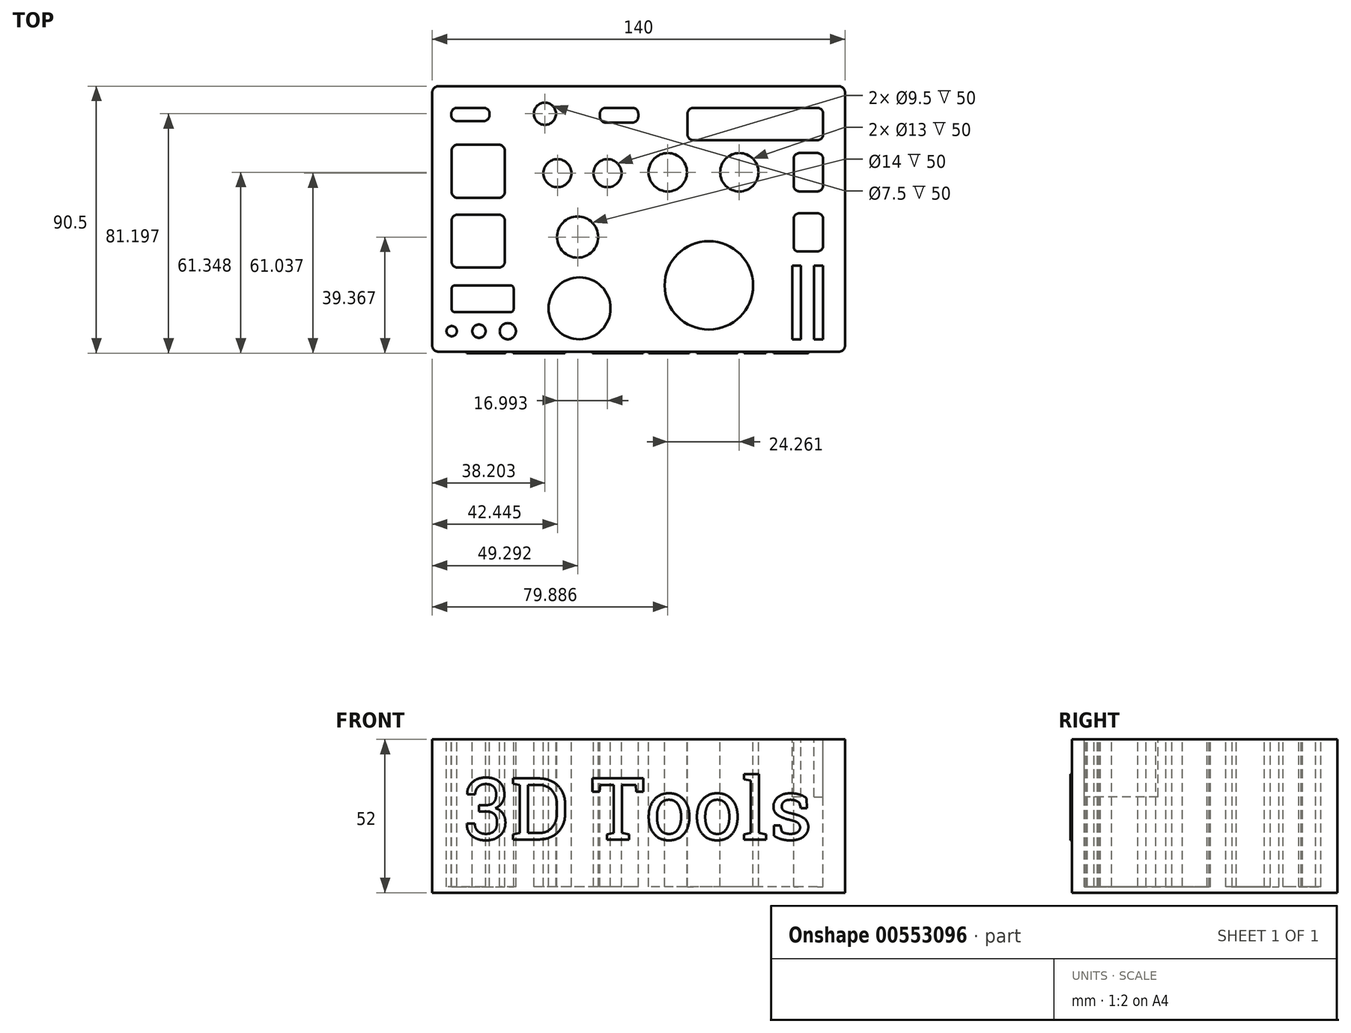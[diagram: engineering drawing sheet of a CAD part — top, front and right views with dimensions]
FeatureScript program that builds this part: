
annotation { "Feature Type Name" : "Feature", "Feature Type Description" : "" }
export const myFeature = defineFeature(function(context is Context, id is Id, definition is map)
    precondition{}
    {
        {
            var Q0;
            Q0=qCreatedBy(makeId("Top.planeOp"),FACE);
            var sketch = newSketch(context, id + "F0", { "sketchPlane" : qUnion([Q0])});
            skLineSegment(sketch, "E0.bottom", {"start": v(-68, 44) * mm, "end": v(68, 44) * mm});
            skLineSegment(sketch, "E0.top", {"start": v(-68, -46) * mm, "end": v(68, -46) * mm});
            skLineSegment(sketch, "E0.left", {"start": v(-70, 42) * mm, "end": v(-70, -44) * mm});
            skLineSegment(sketch, "E0.right", {"start": v(70, 42) * mm, "end": v(70, -44) * mm});
            skCircle(sketch, "E1", {"center": v(-20.04, -31.3) * mm, "radius": 10.5 * mm});
            skLineSegment(sketch, "E2.bottom", {"start": v(60.58, -12.03) * mm, "end": v(54.16, -12.03) * mm});
            skLineSegment(sketch, "E2.top", {"start": v(60.58, 0.97) * mm, "end": v(54.58, 0.97) * mm});
            skLineSegment(sketch, "E2.left", {"start": v(62.58, -10.03) * mm, "end": v(62.58, -1.03) * mm});
            skLineSegment(sketch, "E2.right", {"start": v(52.58, -10.45) * mm, "end": v(52.58, -1.03) * mm});
            skPoint(sketch, "E2.middle", {"position": v(57.58, -5.53) * mm});
            skLineSegment(sketch, "E3.bottom", {"start": v(60.58, 36.7) * mm, "end": v(18.58, 36.7) * mm});
            skLineSegment(sketch, "E3.top", {"start": v(60.58, 25.7) * mm, "end": v(18.58, 25.7) * mm});
            skLineSegment(sketch, "E3.left", {"start": v(62.58, 34.7) * mm, "end": v(62.58, 27.7) * mm});
            skLineSegment(sketch, "E3.right", {"start": v(16.58, 34.7) * mm, "end": v(16.58, 27.7) * mm});
            skPoint(sketch, "E4.visualSharp", {"position": v(16.58, 36.7) * mm});
            skArc(sketch, "E4.filletArc", {"start": v(18.58, 36.7) * mm, "mid": v(17.16, 36.11) * mm, "end": v(16.58, 34.7) * mm});
            skPoint(sketch, "E5.visualSharp", {"position": v(16.58, 25.7) * mm});
            skArc(sketch, "E5.filletArc", {"start": v(16.58, 27.7) * mm, "mid": v(17.16, 26.28) * mm, "end": v(18.58, 25.7) * mm});
            skPoint(sketch, "E6.visualSharp", {"position": v(62.58, 25.7) * mm});
            skArc(sketch, "E6.filletArc", {"start": v(60.58, 25.7) * mm, "mid": v(62, 26.28) * mm, "end": v(62.58, 27.7) * mm});
            skPoint(sketch, "E7.visualSharp", {"position": v(62.58, 36.7) * mm});
            skArc(sketch, "E7.filletArc", {"start": v(62.58, 34.7) * mm, "mid": v(62, 36.11) * mm, "end": v(60.58, 36.7) * mm});
            skPoint(sketch, "E8.visualSharp", {"position": v(62.58, 0.97) * mm});
            skArc(sketch, "E8.filletArc", {"start": v(62.58, -1.03) * mm, "mid": v(62, 0.39) * mm, "end": v(60.58, 0.97) * mm});
            skPoint(sketch, "E9.visualSharp", {"position": v(52.58, 0.97) * mm});
            skArc(sketch, "E9.filletArc", {"start": v(54.58, 0.97) * mm, "mid": v(53.16, 0.39) * mm, "end": v(52.58, -1.03) * mm});
            skPoint(sketch, "E10.visualSharp", {"position": v(52.58, -12.03) * mm});
            skArc(sketch, "E10.filletArc", {"start": v(52.58, -10.45) * mm, "mid": v(53.04, -11.56) * mm, "end": v(54.16, -12.03) * mm});
            skPoint(sketch, "E11.visualSharp", {"position": v(62.58, -12.03) * mm});
            skArc(sketch, "E11.filletArc", {"start": v(60.58, -12.03) * mm, "mid": v(62, -11.44) * mm, "end": v(62.58, -10.03) * mm});
            skPoint(sketch, "E12.visualSharp", {"position": v(-70, 44) * mm});
            skArc(sketch, "E12.filletArc", {"start": v(-68, 44) * mm, "mid": v(-69.41, 43.41) * mm, "end": v(-70, 42) * mm});
            skPoint(sketch, "E13.visualSharp", {"position": v(70, 44) * mm});
            skArc(sketch, "E13.filletArc", {"start": v(70, 42) * mm, "mid": v(69.41, 43.41) * mm, "end": v(68, 44) * mm});
            skPoint(sketch, "E14.endSnap0", {"position": v(52.58, -5.74) * mm});
            skPoint(sketch, "E15.endSnap0", {"position": v(57.58, 0.97) * mm});
            skPoint(sketch, "E16.endSnap0", {"position": v(16.58, 31.2) * mm});
            skCircle(sketch, "E17", {"center": v(-20.7, -7.13) * mm, "radius": 7 * mm});
            skCircle(sketch, "E18", {"center": v(-10.56, 14.54) * mm, "radius": 4.75 * mm});
            skLineSegment(sketch, "E19.bottom", {"start": v(60.58, 8.35) * mm, "end": v(54.58, 8.35) * mm});
            skLineSegment(sketch, "E19.top", {"start": v(60.58, 21.35) * mm, "end": v(54.58, 21.35) * mm});
            skLineSegment(sketch, "E19.left", {"start": v(62.58, 10.35) * mm, "end": v(62.58, 19.35) * mm});
            skLineSegment(sketch, "E19.right", {"start": v(52.58, 10.35) * mm, "end": v(52.58, 19.35) * mm});
            skPoint(sketch, "E20.visualSharp", {"position": v(52.58, 21.35) * mm});
            skArc(sketch, "E20.filletArc", {"start": v(54.58, 21.35) * mm, "mid": v(53.16, 20.76) * mm, "end": v(52.58, 19.35) * mm});
            skPoint(sketch, "E21.visualSharp", {"position": v(62.58, 21.35) * mm});
            skArc(sketch, "E21.filletArc", {"start": v(62.58, 19.35) * mm, "mid": v(62, 20.76) * mm, "end": v(60.58, 21.35) * mm});
            skPoint(sketch, "E22.visualSharp", {"position": v(62.58, 8.35) * mm});
            skArc(sketch, "E22.filletArc", {"start": v(60.58, 8.35) * mm, "mid": v(62, 8.93) * mm, "end": v(62.58, 10.35) * mm});
            skPoint(sketch, "E23.visualSharp", {"position": v(52.58, 8.35) * mm});
            skArc(sketch, "E23.filletArc", {"start": v(52.58, 10.35) * mm, "mid": v(53.16, 8.93) * mm, "end": v(54.58, 8.35) * mm});
            skCircle(sketch, "E24", {"center": v(23.83, -23.52) * mm, "radius": 15 * mm});
            skCircle(sketch, "E25", {"center": v(34.15, 14.85) * mm, "radius": 6.5 * mm});
            skCircle(sketch, "E26", {"center": v(9.89, 14.85) * mm, "radius": 6.5 * mm});
            skCircle(sketch, "E27", {"center": v(-63.43, -39.06) * mm, "radius": 1.75 * mm});
            skLineSegment(sketch, "E28.bottom", {"start": v(-61.43, 0.5) * mm, "end": v(-47.43, 0.5) * mm});
            skLineSegment(sketch, "E28.top", {"start": v(-61.43, -17.5) * mm, "end": v(-47.43, -17.5) * mm});
            skLineSegment(sketch, "E28.left", {"start": v(-63.43, -1.5) * mm, "end": v(-63.43, -15.5) * mm});
            skLineSegment(sketch, "E28.right", {"start": v(-45.43, -1.5) * mm, "end": v(-45.43, -15.5) * mm});
            skPoint(sketch, "E29.visualSharp", {"position": v(-63.43, 0.5) * mm});
            skArc(sketch, "E29.filletArc", {"start": v(-61.43, 0.5) * mm, "mid": v(-62.84, -0.1) * mm, "end": v(-63.43, -1.5) * mm});
            skPoint(sketch, "E30.visualSharp", {"position": v(-63.43, -17.5) * mm});
            skArc(sketch, "E30.filletArc", {"start": v(-63.43, -15.5) * mm, "mid": v(-62.84, -16.92) * mm, "end": v(-61.43, -17.5) * mm});
            skPoint(sketch, "E31.visualSharp", {"position": v(-45.43, -17.5) * mm});
            skArc(sketch, "E31.filletArc", {"start": v(-47.43, -17.5) * mm, "mid": v(-46.01, -16.92) * mm, "end": v(-45.43, -15.5) * mm});
            skPoint(sketch, "E32.visualSharp", {"position": v(-45.43, 0.5) * mm});
            skArc(sketch, "E32.filletArc", {"start": v(-45.43, -1.5) * mm, "mid": v(-46.01, -0.1) * mm, "end": v(-47.43, 0.5) * mm});
            skPoint(sketch, "E33.visualSharp", {"position": v(-70, -46) * mm});
            skArc(sketch, "E33.filletArc", {"start": v(-70, -44) * mm, "mid": v(-69.41, -45.41) * mm, "end": v(-68, -46) * mm});
            skPoint(sketch, "E34.visualSharp", {"position": v(70, -46) * mm});
            skArc(sketch, "E34.filletArc", {"start": v(68, -46) * mm, "mid": v(69.41, -45.41) * mm, "end": v(70, -44) * mm});
            skCircle(sketch, "E35", {"center": v(-54.16, -39.06) * mm, "radius": 2.25 * mm});
            skCircle(sketch, "E36", {"center": v(-44.38, -39.06) * mm, "radius": 2.75 * mm});
            skLineSegment(sketch, "E37.bottom", {"start": v(-61.43, 6.18) * mm, "end": v(-47.43, 6.18) * mm});
            skLineSegment(sketch, "E37.top", {"start": v(-61.43, 24.18) * mm, "end": v(-47.43, 24.18) * mm});
            skLineSegment(sketch, "E37.left", {"start": v(-63.43, 8.18) * mm, "end": v(-63.43, 22.18) * mm});
            skLineSegment(sketch, "E37.right", {"start": v(-45.43, 8.18) * mm, "end": v(-45.43, 22.18) * mm});
            skPoint(sketch, "E38.visualSharp", {"position": v(-63.43, 24.18) * mm});
            skArc(sketch, "E38.filletArc", {"start": v(-61.43, 24.18) * mm, "mid": v(-62.84, 23.6) * mm, "end": v(-63.43, 22.18) * mm});
            skPoint(sketch, "E39.visualSharp", {"position": v(-45.43, 24.18) * mm});
            skArc(sketch, "E39.filletArc", {"start": v(-45.43, 22.18) * mm, "mid": v(-46.01, 23.6) * mm, "end": v(-47.43, 24.18) * mm});
            skPoint(sketch, "E40.visualSharp", {"position": v(-45.43, 6.18) * mm});
            skArc(sketch, "E40.filletArc", {"start": v(-47.43, 6.18) * mm, "mid": v(-46.01, 6.77) * mm, "end": v(-45.43, 8.18) * mm});
            skPoint(sketch, "E41.visualSharp", {"position": v(-63.43, 6.18) * mm});
            skArc(sketch, "E41.filletArc", {"start": v(-63.43, 8.18) * mm, "mid": v(-62.84, 6.77) * mm, "end": v(-61.43, 6.18) * mm});
            skLineSegment(sketch, "E42", {"start": v(62.58, -10.03) * mm, "end": v(62.58, -10.17) * mm, "construction": true});
            skCircle(sketch, "E43", {"center": v(-27.55, 14.54) * mm, "radius": 4.75 * mm});
            skLineSegment(sketch, "E44.bottom", {"start": v(-52.59, 36.7) * mm, "end": v(-61.59, 36.7) * mm});
            skLineSegment(sketch, "E44.top", {"start": v(-52.59, 32.2) * mm, "end": v(-61.59, 32.2) * mm});
            skLineSegment(sketch, "E44.left", {"start": v(-50.59, 34.7) * mm, "end": v(-50.59, 34.2) * mm});
            skLineSegment(sketch, "E44.right", {"start": v(-63.59, 34.7) * mm, "end": v(-63.59, 34.2) * mm});
            skLineSegment(sketch, "E45.bottom", {"start": v(-2.13, 36.7) * mm, "end": v(-11.13, 36.7) * mm});
            skLineSegment(sketch, "E45.top", {"start": v(-2.13, 31.7) * mm, "end": v(-11.13, 31.7) * mm});
            skLineSegment(sketch, "E45.left", {"start": v(-0.13, 34.7) * mm, "end": v(-0.13, 33.7) * mm});
            skLineSegment(sketch, "E45.right", {"start": v(-13.13, 34.7) * mm, "end": v(-13.13, 33.7) * mm});
            skPoint(sketch, "E46.visualSharp", {"position": v(-13.13, 36.7) * mm});
            skArc(sketch, "E46.filletArc", {"start": v(-11.13, 36.7) * mm, "mid": v(-12.54, 36.11) * mm, "end": v(-13.13, 34.7) * mm});
            skPoint(sketch, "E47.visualSharp", {"position": v(-0.13, 36.7) * mm});
            skArc(sketch, "E47.filletArc", {"start": v(-0.13, 34.7) * mm, "mid": v(-0.71, 36.11) * mm, "end": v(-2.13, 36.7) * mm});
            skPoint(sketch, "E48.visualSharp", {"position": v(-0.13, 31.7) * mm});
            skArc(sketch, "E48.filletArc", {"start": v(-2.13, 31.7) * mm, "mid": v(-0.71, 32.28) * mm, "end": v(-0.13, 33.7) * mm});
            skPoint(sketch, "E49.visualSharp", {"position": v(-13.13, 31.7) * mm});
            skArc(sketch, "E49.filletArc", {"start": v(-13.13, 33.7) * mm, "mid": v(-12.54, 32.28) * mm, "end": v(-11.13, 31.7) * mm});
            skPoint(sketch, "E50.visualSharp", {"position": v(-50.59, 36.7) * mm});
            skArc(sketch, "E50.filletArc", {"start": v(-50.59, 34.7) * mm, "mid": v(-51.18, 36.11) * mm, "end": v(-52.59, 36.7) * mm});
            skPoint(sketch, "E51.visualSharp", {"position": v(-63.59, 36.7) * mm});
            skArc(sketch, "E51.filletArc", {"start": v(-61.59, 36.7) * mm, "mid": v(-63, 36.11) * mm, "end": v(-63.59, 34.7) * mm});
            skPoint(sketch, "E52.visualSharp", {"position": v(-63.59, 32.2) * mm});
            skArc(sketch, "E52.filletArc", {"start": v(-63.59, 34.2) * mm, "mid": v(-63, 32.78) * mm, "end": v(-61.59, 32.2) * mm});
            skPoint(sketch, "E53.visualSharp", {"position": v(-50.59, 32.2) * mm});
            skArc(sketch, "E53.filletArc", {"start": v(-52.59, 32.2) * mm, "mid": v(-51.18, 32.78) * mm, "end": v(-50.59, 34.2) * mm});
            skCircle(sketch, "E54", {"center": v(-31.8, 34.7) * mm, "radius": 3.75 * mm});
            skLineSegment(sketch, "E55.bottom", {"start": v(59.48, -16.8) * mm, "end": v(62.48, -16.8) * mm});
            skLineSegment(sketch, "E55.top", {"start": v(59.48, -41.8) * mm, "end": v(62.48, -41.8) * mm});
            skLineSegment(sketch, "E55.left", {"start": v(59.48, -16.8) * mm, "end": v(59.48, -41.8) * mm});
            skLineSegment(sketch, "E55.right", {"start": v(62.48, -16.8) * mm, "end": v(62.48, -41.8) * mm});
            skLineSegment(sketch, "E56.bottom", {"start": v(55.1, -16.8) * mm, "end": v(52.1, -16.8) * mm});
            skLineSegment(sketch, "E56.top", {"start": v(55.1, -41.8) * mm, "end": v(52.1, -41.8) * mm});
            skLineSegment(sketch, "E56.left", {"start": v(55.1, -16.8) * mm, "end": v(55.1, -41.8) * mm});
            skLineSegment(sketch, "E56.right", {"start": v(52.1, -16.8) * mm, "end": v(52.1, -41.8) * mm});
            skCircle(sketch, "E57", {"center": v(23.83, -23.52) * mm, "radius": 18 * mm, "construction": true});
            skLineSegment(sketch, "E58", {"start": v(62.48, -41.8) * mm, "end": v(-65.24, -41.8) * mm, "construction": true});
            skLineSegment(sketch, "E59.bottom", {"start": v(-62.43, -23.57) * mm, "end": v(-43.43, -23.57) * mm});
            skLineSegment(sketch, "E59.top", {"start": v(-62.43, -32.57) * mm, "end": v(-43.43, -32.57) * mm});
            skLineSegment(sketch, "E59.left", {"start": v(-63.43, -24.57) * mm, "end": v(-63.43, -31.57) * mm});
            skLineSegment(sketch, "E59.right", {"start": v(-42.43, -24.57) * mm, "end": v(-42.43, -31.57) * mm});
            skPoint(sketch, "E60.visualSharp", {"position": v(-63.43, -23.57) * mm});
            skArc(sketch, "E60.filletArc", {"start": v(-62.43, -23.57) * mm, "mid": v(-63.13, -23.86) * mm, "end": v(-63.43, -24.57) * mm});
            skPoint(sketch, "E61.visualSharp", {"position": v(-63.43, -32.57) * mm});
            skArc(sketch, "E61.filletArc", {"start": v(-63.43, -31.57) * mm, "mid": v(-63.13, -32.28) * mm, "end": v(-62.43, -32.57) * mm});
            skPoint(sketch, "E62.visualSharp", {"position": v(-42.43, -32.57) * mm});
            skArc(sketch, "E62.filletArc", {"start": v(-43.43, -32.57) * mm, "mid": v(-42.72, -32.28) * mm, "end": v(-42.43, -31.57) * mm});
            skPoint(sketch, "E63.visualSharp", {"position": v(-42.43, -23.57) * mm});
            skArc(sketch, "E63.filletArc", {"start": v(-42.43, -24.57) * mm, "mid": v(-42.72, -23.86) * mm, "end": v(-43.43, -23.57) * mm});
            skSolve(sketch);
        }
        {
            var Q0;
            Q0=makeQuery(id+"F0.imprint","IMPRINT",FACE,{"disambiguationData":[TD([[makeQuery(id+"F0.imprint","IMPRINT",EDGE,{"derivedFrom":sQuery(id+"F0.wireOp",EDGE,"E0.bottom")}),-1.0]])]});
            var Q1;
            Q1=makeQuery(id+"F0.imprint","IMPRINT",FACE,{"disambiguationData":[TD([[makeQuery(id+"F0.imprint","IMPRINT",EDGE,{"derivedFrom":sQuery(id+"F0.wireOp",EDGE,"ee627ebb-3888-4499-a57b-b38a192c3dfd.1.0.2")}),-1.0]])]});
            var Q2;
            Q2=makeQuery(id+"F0.imprint","IMPRINT",FACE,{"disambiguationData":[TD([[makeQuery(id+"F0.imprint","IMPRINT",EDGE,{"derivedFrom":sQuery(id+"F0.wireOp",EDGE,"E17")}),1.0]])]});
            var Q3;
            Q3=makeQuery(id+"F0.imprint","IMPRINT",FACE,{"disambiguationData":[TD([[makeQuery(id+"F0.imprint","IMPRINT",EDGE,{"derivedFrom":sQuery(id+"F0.wireOp",EDGE,"E1")}),1.0]])]});
            var Q4;
            Q4=makeQuery(id+"F0.imprint","IMPRINT",FACE,{"disambiguationData":[TD([[makeQuery(id+"F0.imprint","IMPRINT",EDGE,{"derivedFrom":sQuery(id+"F0.wireOp",EDGE,"E35")}),1.0]])]});
            var Q5;
            Q5=makeQuery(id+"F0.imprint","IMPRINT",FACE,{"disambiguationData":[TD([[makeQuery(id+"F0.imprint","IMPRINT",EDGE,{"derivedFrom":sQuery(id+"F0.wireOp",EDGE,"E27")}),1.0]])]});
            var Q6;
            Q6=makeQuery(id+"F0.imprint","IMPRINT",FACE,{"disambiguationData":[TD([[makeQuery(id+"F0.imprint","IMPRINT",EDGE,{"derivedFrom":sQuery(id+"F0.wireOp",EDGE,"E18")}),1.0]])]});
            var Q7;
            Q7=makeQuery(id+"F0.imprint","IMPRINT",FACE,{"disambiguationData":[TD([[makeQuery(id+"F0.imprint","IMPRINT",EDGE,{"derivedFrom":sQuery(id+"F0.wireOp",EDGE,"E2.bottom")}),-1.0]])]});
            var Q8;
            Q8=makeQuery(id+"F0.imprint","IMPRINT",FACE,{"disambiguationData":[TD([[makeQuery(id+"F0.imprint","IMPRINT",EDGE,{"derivedFrom":sQuery(id+"F0.wireOp",EDGE,"E26")}),1.0]])]});
            var Q9;
            Q9=makeQuery(id+"F0.imprint","IMPRINT",FACE,{"disambiguationData":[TD([[makeQuery(id+"F0.imprint","IMPRINT",EDGE,{"derivedFrom":sQuery(id+"F0.wireOp",EDGE,"E19.bottom")}),-1.0]])]});
            var Q10;
            Q10=makeQuery(id+"F0.imprint","IMPRINT",FACE,{"disambiguationData":[TD([[makeQuery(id+"F0.imprint","IMPRINT",EDGE,{"derivedFrom":sQuery(id+"F0.wireOp",EDGE,"E28.bottom")}),-1.0]])]});
            var Q11;
            Q11=makeQuery(id+"F0.imprint","IMPRINT",FACE,{"disambiguationData":[TD([[makeQuery(id+"F0.imprint","IMPRINT",EDGE,{"derivedFrom":sQuery(id+"F0.wireOp",EDGE,"4a7qP7ZZ-r0X5-byNS-ICWn-bQctXqWbC7CM.bottom")}),-1.0]])]});
            var Q12;
            Q12=makeQuery(id+"F0.imprint","IMPRINT",FACE,{"disambiguationData":[TD([[makeQuery(id+"F0.imprint","IMPRINT",EDGE,{"derivedFrom":sQuery(id+"F0.wireOp",EDGE,"E24")}),1.0]])]});
            var Q13;
            Q13=makeQuery(id+"F0.imprint","IMPRINT",FACE,{"disambiguationData":[TD([[makeQuery(id+"F0.imprint","IMPRINT",EDGE,{"derivedFrom":sQuery(id+"F0.wireOp",EDGE,"E3.bottom")}),1.0]])]});
            var Q14;
            Q14=makeQuery(id+"F0.imprint","IMPRINT",FACE,{"disambiguationData":[TD([[makeQuery(id+"F0.imprint","IMPRINT",EDGE,{"derivedFrom":sQuery(id+"F0.wireOp",EDGE,"E36")}),1.0]])]});
            var Q15;
            Q15=makeQuery(id+"F0.imprint","IMPRINT",FACE,{"disambiguationData":[TD([[makeQuery(id+"F0.imprint","IMPRINT",EDGE,{"derivedFrom":sQuery(id+"F0.wireOp",EDGE,"EhoUKOYd-F9xg-Anw4-pL86-OLlg67FJnalG.bottom")}),-1.0]])]});
            var Q16;
            Q16=makeQuery(id+"F0.imprint","IMPRINT",FACE,{"disambiguationData":[TD([[makeQuery(id+"F0.imprint","IMPRINT",EDGE,{"derivedFrom":sQuery(id+"F0.wireOp",EDGE,"E25")}),1.0]])]});
            var Q17;
            Q17=makeQuery(id+"F0.imprint","IMPRINT",FACE,{"disambiguationData":[TD([[makeQuery(id+"F0.imprint","IMPRINT",EDGE,{"derivedFrom":sQuery(id+"F0.wireOp",EDGE,"464e7144-d0c7-4a8d-839e-04f37b4d9bd1.sketch_text.stroke-82")}),1.0]])]});
            var Q18;
            Q18=makeQuery(id+"F0.imprint","IMPRINT",FACE,{"disambiguationData":[TD([[makeQuery(id+"F0.imprint","IMPRINT",EDGE,{"derivedFrom":sQuery(id+"F0.wireOp",EDGE,"856d63bc-344b-49ef-912d-e5f4858e9d90.sketch_text.stroke-64")}),1.0]])]});
            var Q19;
            Q19=makeQuery(id+"F0.imprint","IMPRINT",FACE,{"disambiguationData":[TD([[makeQuery(id+"F0.imprint","IMPRINT",EDGE,{"derivedFrom":sQuery(id+"F0.wireOp",EDGE,"pRuMvYhj-AQSb-J7kI-29Xz-TcpJe1fpZ1vP.bottom")}),-1.0]])]});
            var Q20;
            Q20=makeQuery(id+"F0.imprint","IMPRINT",FACE,{"disambiguationData":[TD([[makeQuery(id+"F0.imprint","IMPRINT",EDGE,{"derivedFrom":sQuery(id+"F0.wireOp",EDGE,"82b4a819-2965-4918-af0a-af63fe75002e.sketch_text.stroke-41")}),-1.0]])]});
            var Q21;
            Q21=makeQuery(id+"F0.imprint","IMPRINT",FACE,{"disambiguationData":[TD([[makeQuery(id+"F0.imprint","IMPRINT",EDGE,{"derivedFrom":sQuery(id+"F0.wireOp",EDGE,"856d63bc-344b-49ef-912d-e5f4858e9d90.sketch_text.stroke-72")}),-1.0]])]});
            var Q22;
            Q22=makeQuery(id+"F0.imprint","IMPRINT",FACE,{"disambiguationData":[TD([[makeQuery(id+"F0.imprint","IMPRINT",EDGE,{"derivedFrom":sQuery(id+"F0.wireOp",EDGE,"856d63bc-344b-49ef-912d-e5f4858e9d90.sketch_text.stroke-11")}),1.0]])]});
            var Q23;
            Q23=makeQuery(id+"F0.imprint","IMPRINT",FACE,{"disambiguationData":[TD([[makeQuery(id+"F0.imprint","IMPRINT",EDGE,{"derivedFrom":sQuery(id+"F0.wireOp",EDGE,"5b80845d-3cdb-4e32-9a99-3b0762a64691.sketch_text.stroke-89")}),-1.0]])]});
            var Q24;
            Q24=makeQuery(id+"F0.imprint","IMPRINT",FACE,{"disambiguationData":[TD([[makeQuery(id+"F0.imprint","IMPRINT",EDGE,{"derivedFrom":sQuery(id+"F0.wireOp",EDGE,"dd86ef6c-a984-4585-901d-e8c8913c4099.sketch_text.stroke-55")}),-1.0]])]});
            var Q25;
            Q25=makeQuery(id+"F0.imprint","IMPRINT",FACE,{"disambiguationData":[TD([[makeQuery(id+"F0.imprint","IMPRINT",EDGE,{"derivedFrom":sQuery(id+"F0.wireOp",EDGE,"d4bc6b6e-f296-4560-aa30-6e7daed0d7fc.sketch_text.stroke-0")}),-1.0]])]});
            var Q26;
            Q26=makeQuery(id+"F0.imprint","IMPRINT",FACE,{"disambiguationData":[TD([[makeQuery(id+"F0.imprint","IMPRINT",EDGE,{"derivedFrom":sQuery(id+"F0.wireOp",EDGE,"f59299c1-d707-4fe5-9817-1f4a215b2932.sketch_text.stroke-45")}),-1.0]])]});
            var Q27;
            Q27=makeQuery(id+"F0.imprint","IMPRINT",FACE,{"disambiguationData":[TD([[makeQuery(id+"F0.imprint","IMPRINT",EDGE,{"derivedFrom":sQuery(id+"F0.wireOp",EDGE,"82b4a819-2965-4918-af0a-af63fe75002e.sketch_text.stroke-0")}),-1.0]])]});
            var Q28;
            Q28=makeQuery(id+"F0.imprint","IMPRINT",FACE,{"disambiguationData":[TD([[makeQuery(id+"F0.imprint","IMPRINT",EDGE,{"derivedFrom":sQuery(id+"F0.wireOp",EDGE,"856d63bc-344b-49ef-912d-e5f4858e9d90.sketch_text.stroke-55")}),-1.0]])]});
            var Q29;
            Q29=makeQuery(id+"F0.imprint","IMPRINT",FACE,{"disambiguationData":[TD([[makeQuery(id+"F0.imprint","IMPRINT",EDGE,{"derivedFrom":sQuery(id+"F0.wireOp",EDGE,"82b4a819-2965-4918-af0a-af63fe75002e.sketch_text.stroke-20")}),-1.0]])]});
            var Q30;
            Q30=makeQuery(id+"F0.imprint","IMPRINT",FACE,{"disambiguationData":[TD([[makeQuery(id+"F0.imprint","IMPRINT",EDGE,{"derivedFrom":sQuery(id+"F0.wireOp",EDGE,"f59299c1-d707-4fe5-9817-1f4a215b2932.sketch_text.stroke-58")}),-1.0]])]});
            var Q31;
            Q31=makeQuery(id+"F0.imprint","IMPRINT",FACE,{"disambiguationData":[TD([[makeQuery(id+"F0.imprint","IMPRINT",EDGE,{"derivedFrom":sQuery(id+"F0.wireOp",EDGE,"464e7144-d0c7-4a8d-839e-04f37b4d9bd1.sketch_text.stroke-12")}),-1.0]])]});
            var Q32;
            Q32=makeQuery(id+"F0.imprint","IMPRINT",FACE,{"disambiguationData":[TD([[makeQuery(id+"F0.imprint","IMPRINT",EDGE,{"derivedFrom":sQuery(id+"F0.wireOp",EDGE,"b7b5839e-f96e-4560-91f1-7bf6c6787ae4.sketch_text.stroke-0")}),-1.0]])]});
            var Q33;
            Q33=makeQuery(id+"F0.imprint","IMPRINT",FACE,{"disambiguationData":[TD([[makeQuery(id+"F0.imprint","IMPRINT",EDGE,{"derivedFrom":sQuery(id+"F0.wireOp",EDGE,"2062883b-def4-4ea2-a975-12661bf533bd.sketch_text.stroke-45")}),-1.0]])]});
            var Q34;
            Q34=makeQuery(id+"F0.imprint","IMPRINT",FACE,{"disambiguationData":[TD([[makeQuery(id+"F0.imprint","IMPRINT",EDGE,{"derivedFrom":sQuery(id+"F0.wireOp",EDGE,"f59299c1-d707-4fe5-9817-1f4a215b2932.sketch_text.stroke-0")}),-1.0]])]});
            var Q35;
            Q35=makeQuery(id+"F0.imprint","IMPRINT",FACE,{"disambiguationData":[TD([[makeQuery(id+"F0.imprint","IMPRINT",EDGE,{"derivedFrom":sQuery(id+"F0.wireOp",EDGE,"464e7144-d0c7-4a8d-839e-04f37b4d9bd1.sketch_text.stroke-39")}),-1.0]])]});
            var Q36;
            Q36=makeQuery(id+"F0.imprint","IMPRINT",FACE,{"disambiguationData":[TD([[makeQuery(id+"F0.imprint","IMPRINT",EDGE,{"derivedFrom":sQuery(id+"F0.wireOp",EDGE,"5b80845d-3cdb-4e32-9a99-3b0762a64691.sketch_text.stroke-70")}),-1.0]])]});
            var Q37;
            Q37=makeQuery(id+"F0.imprint","IMPRINT",FACE,{"disambiguationData":[TD([[makeQuery(id+"F0.imprint","IMPRINT",EDGE,{"derivedFrom":sQuery(id+"F0.wireOp",EDGE,"dd86ef6c-a984-4585-901d-e8c8913c4099.sketch_text.stroke-38")}),-1.0]])]});
            var Q38;
            Q38=makeQuery(id+"F0.imprint","IMPRINT",FACE,{"disambiguationData":[TD([[makeQuery(id+"F0.imprint","IMPRINT",EDGE,{"derivedFrom":sQuery(id+"F0.wireOp",EDGE,"856d63bc-344b-49ef-912d-e5f4858e9d90.sketch_text.stroke-0")}),-1.0]])]});
            var Q39;
            Q39=makeQuery(id+"F0.imprint","IMPRINT",FACE,{"disambiguationData":[TD([[makeQuery(id+"F0.imprint","IMPRINT",EDGE,{"derivedFrom":sQuery(id+"F0.wireOp",EDGE,"dd86ef6c-a984-4585-901d-e8c8913c4099.sketch_text.stroke-8")}),-1.0]])]});
            var Q40;
            Q40=makeQuery(id+"F0.imprint","IMPRINT",FACE,{"disambiguationData":[TD([[makeQuery(id+"F0.imprint","IMPRINT",EDGE,{"derivedFrom":sQuery(id+"F0.wireOp",EDGE,"7fa3139a-55d7-4135-be88-2865c4e3e1c7.sketch_text.stroke-39")}),-1.0]])]});
            var Q41;
            Q41=makeQuery(id+"F0.imprint","IMPRINT",FACE,{"disambiguationData":[TD([[makeQuery(id+"F0.imprint","IMPRINT",EDGE,{"derivedFrom":sQuery(id+"F0.wireOp",EDGE,"922ba498-ed72-4b5b-995e-0f6d56ec32e2.sketch_text.stroke-66")}),-1.0]])]});
            var Q42;
            Q42=makeQuery(id+"F0.imprint","IMPRINT",FACE,{"disambiguationData":[TD([[makeQuery(id+"F0.imprint","IMPRINT",EDGE,{"derivedFrom":sQuery(id+"F0.wireOp",EDGE,"922ba498-ed72-4b5b-995e-0f6d56ec32e2.sketch_text.stroke-14")}),-1.0]])]});
            var Q43;
            Q43=makeQuery(id+"F0.imprint","IMPRINT",FACE,{"disambiguationData":[TD([[makeQuery(id+"F0.imprint","IMPRINT",EDGE,{"derivedFrom":sQuery(id+"F0.wireOp",EDGE,"922ba498-ed72-4b5b-995e-0f6d56ec32e2.sketch_text.stroke-10")}),-1.0]])]});
            var Q44;
            Q44=makeQuery(id+"F0.imprint","IMPRINT",FACE,{"disambiguationData":[TD([[makeQuery(id+"F0.imprint","IMPRINT",EDGE,{"derivedFrom":sQuery(id+"F0.wireOp",EDGE,"859a48e1-c7f7-4a18-9492-87fe2e6c1c5c.sketch_text.stroke-15")}),-1.0]])]});
            var Q45;
            Q45=makeQuery(id+"F0.imprint","IMPRINT",FACE,{"disambiguationData":[TD([[makeQuery(id+"F0.imprint","IMPRINT",EDGE,{"derivedFrom":sQuery(id+"F0.wireOp",EDGE,"856d63bc-344b-49ef-912d-e5f4858e9d90.sketch_text.stroke-45")}),-1.0]])]});
            var Q46;
            Q46=makeQuery(id+"F0.imprint","IMPRINT",FACE,{"disambiguationData":[TD([[makeQuery(id+"F0.imprint","IMPRINT",EDGE,{"derivedFrom":sQuery(id+"F0.wireOp",EDGE,"7fa3139a-55d7-4135-be88-2865c4e3e1c7.sketch_text.stroke-0")}),-1.0]])]});
            var Q47;
            Q47=makeQuery(id+"F0.imprint","IMPRINT",FACE,{"disambiguationData":[TD([[makeQuery(id+"F0.imprint","IMPRINT",EDGE,{"derivedFrom":sQuery(id+"F0.wireOp",EDGE,"d4bc6b6e-f296-4560-aa30-6e7daed0d7fc.sketch_text.stroke-56")}),-1.0]])]});
            var Q48;
            Q48=makeQuery(id+"F0.imprint","IMPRINT",FACE,{"disambiguationData":[TD([[makeQuery(id+"F0.imprint","IMPRINT",EDGE,{"derivedFrom":sQuery(id+"F0.wireOp",EDGE,"464e7144-d0c7-4a8d-839e-04f37b4d9bd1.sketch_text.stroke-0")}),-1.0]])]});
            var Q49;
            Q49=makeQuery(id+"F0.imprint","IMPRINT",FACE,{"disambiguationData":[TD([[makeQuery(id+"F0.imprint","IMPRINT",EDGE,{"derivedFrom":sQuery(id+"F0.wireOp",EDGE,"464e7144-d0c7-4a8d-839e-04f37b4d9bd1.sketch_text.stroke-54")}),-1.0]])]});
            var Q50;
            Q50=makeQuery(id+"F0.imprint","IMPRINT",FACE,{"disambiguationData":[TD([[makeQuery(id+"F0.imprint","IMPRINT",EDGE,{"derivedFrom":sQuery(id+"F0.wireOp",EDGE,"dd86ef6c-a984-4585-901d-e8c8913c4099.sketch_text.stroke-0")}),-1.0]])]});
            var Q51;
            Q51=makeQuery(id+"F0.imprint","IMPRINT",FACE,{"disambiguationData":[TD([[makeQuery(id+"F0.imprint","IMPRINT",EDGE,{"derivedFrom":sQuery(id+"F0.wireOp",EDGE,"922ba498-ed72-4b5b-995e-0f6d56ec32e2.sketch_text.stroke-88")}),-1.0]])]});
            var Q52;
            Q52=makeQuery(id+"F0.imprint","IMPRINT",FACE,{"disambiguationData":[TD([[makeQuery(id+"F0.imprint","IMPRINT",EDGE,{"derivedFrom":sQuery(id+"F0.wireOp",EDGE,"bde91d3f-1bd3-45ad-82db-db1f5e1f2c44.sketch_text.stroke-10")}),-1.0]])]});
            var Q53;
            Q53=makeQuery(id+"F0.imprint","IMPRINT",FACE,{"disambiguationData":[TD([[makeQuery(id+"F0.imprint","IMPRINT",EDGE,{"derivedFrom":sQuery(id+"F0.wireOp",EDGE,"5b80845d-3cdb-4e32-9a99-3b0762a64691.sketch_text.stroke-51")}),-1.0]])]});
            var Q54;
            Q54=makeQuery(id+"F0.imprint","IMPRINT",FACE,{"disambiguationData":[TD([[makeQuery(id+"F0.imprint","IMPRINT",EDGE,{"derivedFrom":sQuery(id+"F0.wireOp",EDGE,"d4bc6b6e-f296-4560-aa30-6e7daed0d7fc.sketch_text.stroke-71")}),1.0]])]});
            var Q55;
            Q55=makeQuery(id+"F0.imprint","IMPRINT",FACE,{"disambiguationData":[TD([[makeQuery(id+"F0.imprint","IMPRINT",EDGE,{"derivedFrom":sQuery(id+"F0.wireOp",EDGE,"5b80845d-3cdb-4e32-9a99-3b0762a64691.sketch_text.stroke-15")}),-1.0]])]});
            var Q56;
            Q56=makeQuery(id+"F0.imprint","IMPRINT",FACE,{"disambiguationData":[TD([[makeQuery(id+"F0.imprint","IMPRINT",EDGE,{"derivedFrom":sQuery(id+"F0.wireOp",EDGE,"b7b5839e-f96e-4560-91f1-7bf6c6787ae4.sketch_text.stroke-61")}),-1.0]])]});
            var Q57;
            Q57=makeQuery(id+"F0.imprint","IMPRINT",FACE,{"disambiguationData":[TD([[makeQuery(id+"F0.imprint","IMPRINT",EDGE,{"derivedFrom":sQuery(id+"F0.wireOp",EDGE,"856d63bc-344b-49ef-912d-e5f4858e9d90.sketch_text.stroke-37")}),1.0]])]});
            var Q58;
            Q58=makeQuery(id+"F0.imprint","IMPRINT",FACE,{"disambiguationData":[TD([[makeQuery(id+"F0.imprint","IMPRINT",EDGE,{"derivedFrom":sQuery(id+"F0.wireOp",EDGE,"2062883b-def4-4ea2-a975-12661bf533bd.sketch_text.stroke-58")}),-1.0]])]});
            var Q59;
            Q59=makeQuery(id+"F0.imprint","IMPRINT",FACE,{"disambiguationData":[TD([[makeQuery(id+"F0.imprint","IMPRINT",EDGE,{"derivedFrom":sQuery(id+"F0.wireOp",EDGE,"b7b5839e-f96e-4560-91f1-7bf6c6787ae4.sketch_text.stroke-25")}),-1.0]])]});
            var Q60;
            Q60=makeQuery(id+"F0.imprint","IMPRINT",FACE,{"disambiguationData":[TD([[makeQuery(id+"F0.imprint","IMPRINT",EDGE,{"derivedFrom":sQuery(id+"F0.wireOp",EDGE,"2062883b-def4-4ea2-a975-12661bf533bd.sketch_text.stroke-0")}),-1.0]])]});
            var Q61;
            Q61=makeQuery(id+"F0.imprint","IMPRINT",FACE,{"disambiguationData":[TD([[makeQuery(id+"F0.imprint","IMPRINT",EDGE,{"derivedFrom":sQuery(id+"F0.wireOp",EDGE,"f59299c1-d707-4fe5-9817-1f4a215b2932.sketch_text.stroke-18")}),-1.0]])]});
            var Q62;
            Q62=makeQuery(id+"F0.imprint","IMPRINT",FACE,{"disambiguationData":[TD([[makeQuery(id+"F0.imprint","IMPRINT",EDGE,{"derivedFrom":sQuery(id+"F0.wireOp",EDGE,"d4bc6b6e-f296-4560-aa30-6e7daed0d7fc.sketch_text.stroke-80")}),-1.0]])]});
            var Q63;
            Q63=makeQuery(id+"F0.imprint","IMPRINT",FACE,{"disambiguationData":[TD([[makeQuery(id+"F0.imprint","IMPRINT",EDGE,{"derivedFrom":sQuery(id+"F0.wireOp",EDGE,"859a48e1-c7f7-4a18-9492-87fe2e6c1c5c.sketch_text.stroke-58")}),-1.0]])]});
            var Q64;
            Q64=makeQuery(id+"F0.imprint","IMPRINT",FACE,{"disambiguationData":[TD([[makeQuery(id+"F0.imprint","IMPRINT",EDGE,{"derivedFrom":sQuery(id+"F0.wireOp",EDGE,"bde91d3f-1bd3-45ad-82db-db1f5e1f2c44.sketch_text.stroke-45")}),-1.0]])]});
            var Q65;
            Q65=makeQuery(id+"F0.imprint","IMPRINT",FACE,{"disambiguationData":[TD([[makeQuery(id+"F0.imprint","IMPRINT",EDGE,{"derivedFrom":sQuery(id+"F0.wireOp",EDGE,"7fa3139a-55d7-4135-be88-2865c4e3e1c7.sketch_text.stroke-12")}),-1.0]])]});
            var Q66;
            Q66=makeQuery(id+"F0.imprint","IMPRINT",FACE,{"disambiguationData":[TD([[makeQuery(id+"F0.imprint","IMPRINT",EDGE,{"derivedFrom":sQuery(id+"F0.wireOp",EDGE,"5b80845d-3cdb-4e32-9a99-3b0762a64691.sketch_text.stroke-0")}),-1.0]])]});
            var Q67;
            Q67=makeQuery(id+"F0.imprint","IMPRINT",FACE,{"disambiguationData":[TD([[makeQuery(id+"F0.imprint","IMPRINT",EDGE,{"derivedFrom":sQuery(id+"F0.wireOp",EDGE,"bde91d3f-1bd3-45ad-82db-db1f5e1f2c44.sketch_text.stroke-22")}),-1.0]])]});
            var Q68;
            Q68=makeQuery(id+"F0.imprint","IMPRINT",FACE,{"disambiguationData":[TD([[makeQuery(id+"F0.imprint","IMPRINT",EDGE,{"derivedFrom":sQuery(id+"F0.wireOp",EDGE,"922ba498-ed72-4b5b-995e-0f6d56ec32e2.sketch_text.stroke-144")}),-1.0]])]});
            var Q69;
            Q69=makeQuery(id+"F0.imprint","IMPRINT",FACE,{"disambiguationData":[TD([[makeQuery(id+"F0.imprint","IMPRINT",EDGE,{"derivedFrom":sQuery(id+"F0.wireOp",EDGE,"856d63bc-344b-49ef-912d-e5f4858e9d90.sketch_text.stroke-18")}),-1.0]])]});
            var Q70;
            Q70=makeQuery(id+"F0.imprint","IMPRINT",FACE,{"disambiguationData":[TD([[makeQuery(id+"F0.imprint","IMPRINT",EDGE,{"derivedFrom":sQuery(id+"F0.wireOp",EDGE,"922ba498-ed72-4b5b-995e-0f6d56ec32e2.sketch_text.stroke-84")}),-1.0]])]});
            var Q71;
            Q71=makeQuery(id+"F0.imprint","IMPRINT",FACE,{"disambiguationData":[TD([[makeQuery(id+"F0.imprint","IMPRINT",EDGE,{"derivedFrom":sQuery(id+"F0.wireOp",EDGE,"859a48e1-c7f7-4a18-9492-87fe2e6c1c5c.sketch_text.stroke-31")}),-1.0]])]});
            var Q72;
            Q72=makeQuery(id+"F0.imprint","IMPRINT",FACE,{"disambiguationData":[TD([[makeQuery(id+"F0.imprint","IMPRINT",EDGE,{"derivedFrom":sQuery(id+"F0.wireOp",EDGE,"5b80845d-3cdb-4e32-9a99-3b0762a64691.sketch_text.stroke-32")}),-1.0]])]});
            var Q73;
            Q73=makeQuery(id+"F0.imprint","IMPRINT",FACE,{"disambiguationData":[TD([[makeQuery(id+"F0.imprint","IMPRINT",EDGE,{"derivedFrom":sQuery(id+"F0.wireOp",EDGE,"2062883b-def4-4ea2-a975-12661bf533bd.sketch_text.stroke-73")}),-1.0]])]});
            var Q74;
            Q74=makeQuery(id+"F0.imprint","IMPRINT",FACE,{"disambiguationData":[TD([[makeQuery(id+"F0.imprint","IMPRINT",EDGE,{"derivedFrom":sQuery(id+"F0.wireOp",EDGE,"b7b5839e-f96e-4560-91f1-7bf6c6787ae4.sketch_text.stroke-44")}),-1.0]])]});
            var Q75;
            Q75=makeQuery(id+"F0.imprint","IMPRINT",FACE,{"disambiguationData":[TD([[makeQuery(id+"F0.imprint","IMPRINT",EDGE,{"derivedFrom":sQuery(id+"F0.wireOp",EDGE,"859a48e1-c7f7-4a18-9492-87fe2e6c1c5c.sketch_text.stroke-0")}),-1.0]])]});
            var Q76;
            Q76=makeQuery(id+"F0.imprint","IMPRINT",FACE,{"disambiguationData":[TD([[makeQuery(id+"F0.imprint","IMPRINT",EDGE,{"derivedFrom":sQuery(id+"F0.wireOp",EDGE,"922ba498-ed72-4b5b-995e-0f6d56ec32e2.sketch_text.stroke-41")}),-1.0]])]});
            var Q77;
            Q77=makeQuery(id+"F0.imprint","IMPRINT",FACE,{"disambiguationData":[TD([[makeQuery(id+"F0.imprint","IMPRINT",EDGE,{"derivedFrom":sQuery(id+"F0.wireOp",EDGE,"d4bc6b6e-f296-4560-aa30-6e7daed0d7fc.sketch_text.stroke-29")}),-1.0]])]});
            var Q78;
            Q78=makeQuery(id+"F0.imprint","IMPRINT",FACE,{"disambiguationData":[TD([[makeQuery(id+"F0.imprint","IMPRINT",EDGE,{"derivedFrom":sQuery(id+"F0.wireOp",EDGE,"f59299c1-d707-4fe5-9817-1f4a215b2932.sketch_text.stroke-73")}),-1.0]])]});
            var Q79;
            Q79=makeQuery(id+"F0.imprint","IMPRINT",FACE,{"disambiguationData":[TD([[makeQuery(id+"F0.imprint","IMPRINT",EDGE,{"derivedFrom":sQuery(id+"F0.wireOp",EDGE,"859a48e1-c7f7-4a18-9492-87fe2e6c1c5c.sketch_text.stroke-23")}),-1.0]])]});
            var Q80;
            Q80=makeQuery(id+"F0.imprint","IMPRINT",FACE,{"disambiguationData":[TD([[makeQuery(id+"F0.imprint","IMPRINT",EDGE,{"derivedFrom":sQuery(id+"F0.wireOp",EDGE,"d4bc6b6e-f296-4560-aa30-6e7daed0d7fc.sketch_text.stroke-99")}),-1.0]])]});
            var Q81;
            Q81=makeQuery(id+"F0.imprint","IMPRINT",FACE,{"disambiguationData":[TD([[makeQuery(id+"F0.imprint","IMPRINT",EDGE,{"derivedFrom":sQuery(id+"F0.wireOp",EDGE,"bde91d3f-1bd3-45ad-82db-db1f5e1f2c44.sketch_text.stroke-26")}),-1.0]])]});
            var Q82;
            Q82=makeQuery(id+"F0.imprint","IMPRINT",FACE,{"disambiguationData":[TD([[makeQuery(id+"F0.imprint","IMPRINT",EDGE,{"derivedFrom":sQuery(id+"F0.wireOp",EDGE,"bde91d3f-1bd3-45ad-82db-db1f5e1f2c44.sketch_text.stroke-14")}),-1.0]])]});
            var Q83;
            Q83=makeQuery(id+"F0.imprint","IMPRINT",FACE,{"disambiguationData":[TD([[makeQuery(id+"F0.imprint","IMPRINT",EDGE,{"derivedFrom":sQuery(id+"F0.wireOp",EDGE,"7fa3139a-55d7-4135-be88-2865c4e3e1c7.sketch_text.stroke-31")}),1.0]])]});
            var Q84;
            Q84=makeQuery(id+"F0.imprint","IMPRINT",FACE,{"disambiguationData":[TD([[makeQuery(id+"F0.imprint","IMPRINT",EDGE,{"derivedFrom":sQuery(id+"F0.wireOp",EDGE,"859a48e1-c7f7-4a18-9492-87fe2e6c1c5c.sketch_text.stroke-19")}),-1.0]])]});
            var Q85;
            Q85=makeQuery(id+"F0.imprint","IMPRINT",FACE,{"disambiguationData":[TD([[makeQuery(id+"F0.imprint","IMPRINT",EDGE,{"derivedFrom":sQuery(id+"F0.wireOp",EDGE,"d4bc6b6e-f296-4560-aa30-6e7daed0d7fc.sketch_text.stroke-94")}),1.0]])]});
            var Q86;
            Q86=makeQuery(id+"F0.imprint","IMPRINT",FACE,{"disambiguationData":[TD([[makeQuery(id+"F0.imprint","IMPRINT",EDGE,{"derivedFrom":sQuery(id+"F0.wireOp",EDGE,"f59299c1-d707-4fe5-9817-1f4a215b2932.sketch_text.stroke-87")}),1.0]])]});
            var Q87;
            Q87=makeQuery(id+"F0.imprint","IMPRINT",FACE,{"disambiguationData":[TD([[makeQuery(id+"F0.imprint","IMPRINT",EDGE,{"derivedFrom":sQuery(id+"F0.wireOp",EDGE,"82b4a819-2965-4918-af0a-af63fe75002e.sketch_text.stroke-55")}),1.0]])]});
            var Q88;
            Q88=makeQuery(id+"F0.imprint","IMPRINT",FACE,{"disambiguationData":[TD([[makeQuery(id+"F0.imprint","IMPRINT",EDGE,{"derivedFrom":sQuery(id+"F0.wireOp",EDGE,"f59299c1-d707-4fe5-9817-1f4a215b2932.sketch_text.stroke-37")}),1.0]])]});
            var Q89;
            Q89=makeQuery(id+"F0.imprint","IMPRINT",FACE,{"disambiguationData":[TD([[makeQuery(id+"F0.imprint","IMPRINT",EDGE,{"derivedFrom":sQuery(id+"F0.wireOp",EDGE,"7fa3139a-55d7-4135-be88-2865c4e3e1c7.sketch_text.stroke-73")}),-1.0]])]});
            var Q90;
            Q90=makeQuery(id+"F0.imprint","IMPRINT",FACE,{"disambiguationData":[TD([[makeQuery(id+"F0.imprint","IMPRINT",EDGE,{"derivedFrom":sQuery(id+"F0.wireOp",EDGE,"dd86ef6c-a984-4585-901d-e8c8913c4099.sketch_text.stroke-99")}),-1.0]])]});
            var Q91;
            Q91=makeQuery(id+"F0.imprint","IMPRINT",FACE,{"disambiguationData":[TD([[makeQuery(id+"F0.imprint","IMPRINT",EDGE,{"derivedFrom":sQuery(id+"F0.wireOp",EDGE,"5b80845d-3cdb-4e32-9a99-3b0762a64691.sketch_text.stroke-84")}),1.0]])]});
            var Q92;
            Q92=makeQuery(id+"F0.imprint","IMPRINT",FACE,{"disambiguationData":[TD([[makeQuery(id+"F0.imprint","IMPRINT",EDGE,{"derivedFrom":sQuery(id+"F0.wireOp",EDGE,"5b80845d-3cdb-4e32-9a99-3b0762a64691.sketch_text.stroke-102")}),-1.0]])]});
            var Q93;
            Q93=makeQuery(id+"F0.imprint","IMPRINT",FACE,{"disambiguationData":[TD([[makeQuery(id+"F0.imprint","IMPRINT",EDGE,{"derivedFrom":sQuery(id+"F0.wireOp",EDGE,"dd86ef6c-a984-4585-901d-e8c8913c4099.sketch_text.stroke-26")}),-1.0]])]});
            var Q94;
            Q94=makeQuery(id+"F0.imprint","IMPRINT",FACE,{"disambiguationData":[TD([[makeQuery(id+"F0.imprint","IMPRINT",EDGE,{"derivedFrom":sQuery(id+"F0.wireOp",EDGE,"464e7144-d0c7-4a8d-839e-04f37b4d9bd1.sketch_text.stroke-31")}),1.0]])]});
            var Q95;
            Q95=makeQuery(id+"F0.imprint","IMPRINT",FACE,{"disambiguationData":[TD([[makeQuery(id+"F0.imprint","IMPRINT",EDGE,{"derivedFrom":sQuery(id+"F0.wireOp",EDGE,"922ba498-ed72-4b5b-995e-0f6d56ec32e2.sketch_text.stroke-100")}),-1.0]])]});
            var Q96;
            Q96=makeQuery(id+"F0.imprint","IMPRINT",FACE,{"disambiguationData":[TD([[makeQuery(id+"F0.imprint","IMPRINT",EDGE,{"derivedFrom":sQuery(id+"F0.wireOp",EDGE,"464e7144-d0c7-4a8d-839e-04f37b4d9bd1.sketch_text.stroke-73")}),-1.0]])]});
            var Q97;
            Q97=makeQuery(id+"F0.imprint","IMPRINT",FACE,{"disambiguationData":[TD([[makeQuery(id+"F0.imprint","IMPRINT",EDGE,{"derivedFrom":sQuery(id+"F0.wireOp",EDGE,"b7b5839e-f96e-4560-91f1-7bf6c6787ae4.sketch_text.stroke-78")}),-1.0]])]});
            var Q98;
            Q98=makeQuery(id+"F0.imprint","IMPRINT",FACE,{"disambiguationData":[TD([[makeQuery(id+"F0.imprint","IMPRINT",EDGE,{"derivedFrom":sQuery(id+"F0.wireOp",EDGE,"d4bc6b6e-f296-4560-aa30-6e7daed0d7fc.sketch_text.stroke-11")}),1.0]])]});
            var Q99;
            Q99=makeQuery(id+"F0.imprint","IMPRINT",FACE,{"disambiguationData":[TD([[makeQuery(id+"F0.imprint","IMPRINT",EDGE,{"derivedFrom":sQuery(id+"F0.wireOp",EDGE,"d4bc6b6e-f296-4560-aa30-6e7daed0d7fc.sketch_text.stroke-25")}),-1.0]])]});
            var Q100;
            Q100=makeQuery(id+"F0.imprint","IMPRINT",FACE,{"disambiguationData":[TD([[makeQuery(id+"F0.imprint","IMPRINT",EDGE,{"derivedFrom":sQuery(id+"F0.wireOp",EDGE,"dd86ef6c-a984-4585-901d-e8c8913c4099.sketch_text.stroke-84")}),1.0]])]});
            var Q101;
            Q101=makeQuery(id+"F0.imprint","IMPRINT",FACE,{"disambiguationData":[TD([[makeQuery(id+"F0.imprint","IMPRINT",EDGE,{"derivedFrom":sQuery(id+"F0.wireOp",EDGE,"859a48e1-c7f7-4a18-9492-87fe2e6c1c5c.sketch_text.stroke-71")}),-1.0]])]});
            var Q102;
            Q102=makeQuery(id+"F0.imprint","IMPRINT",FACE,{"disambiguationData":[TD([[makeQuery(id+"F0.imprint","IMPRINT",EDGE,{"derivedFrom":sQuery(id+"F0.wireOp",EDGE,"2062883b-def4-4ea2-a975-12661bf533bd.sketch_text.stroke-92")}),-1.0]])]});
            var Q103;
            Q103=makeQuery(id+"F0.imprint","IMPRINT",FACE,{"disambiguationData":[TD([[makeQuery(id+"F0.imprint","IMPRINT",EDGE,{"derivedFrom":sQuery(id+"F0.wireOp",EDGE,"922ba498-ed72-4b5b-995e-0f6d56ec32e2.sketch_text.stroke-162")}),-1.0]])]});
            var Q104;
            Q104=makeQuery(id+"F0.imprint","IMPRINT",FACE,{"disambiguationData":[TD([[makeQuery(id+"F0.imprint","IMPRINT",EDGE,{"derivedFrom":sQuery(id+"F0.wireOp",EDGE,"f59299c1-d707-4fe5-9817-1f4a215b2932.sketch_text.stroke-92")}),-1.0]])]});
            var Q105;
            Q105=makeQuery(id+"F0.imprint","IMPRINT",FACE,{"disambiguationData":[TD([[makeQuery(id+"F0.imprint","IMPRINT",EDGE,{"derivedFrom":sQuery(id+"F0.wireOp",EDGE,"859a48e1-c7f7-4a18-9492-87fe2e6c1c5c.sketch_text.stroke-50")}),1.0]])]});
            var Q106;
            Q106=makeQuery(id+"F0.imprint","IMPRINT",FACE,{"disambiguationData":[TD([[makeQuery(id+"F0.imprint","IMPRINT",EDGE,{"derivedFrom":sQuery(id+"F0.wireOp",EDGE,"7fa3139a-55d7-4135-be88-2865c4e3e1c7.sketch_text.stroke-54")}),-1.0]])]});
            var Q107;
            Q107=makeQuery(id+"F0.imprint","IMPRINT",FACE,{"disambiguationData":[TD([[makeQuery(id+"F0.imprint","IMPRINT",EDGE,{"derivedFrom":sQuery(id+"F0.wireOp",EDGE,"2062883b-def4-4ea2-a975-12661bf533bd.sketch_text.stroke-87")}),1.0]])]});
            var Q108;
            Q108=makeQuery(id+"F0.imprint","IMPRINT",FACE,{"disambiguationData":[TD([[makeQuery(id+"F0.imprint","IMPRINT",EDGE,{"derivedFrom":sQuery(id+"F0.wireOp",EDGE,"922ba498-ed72-4b5b-995e-0f6d56ec32e2.sketch_text.stroke-0")}),-1.0]])]});
            var Q109;
            Q109=makeQuery(id+"F0.imprint","IMPRINT",FACE,{"disambiguationData":[TD([[makeQuery(id+"F0.imprint","IMPRINT",EDGE,{"derivedFrom":sQuery(id+"F0.wireOp",EDGE,"7fa3139a-55d7-4135-be88-2865c4e3e1c7.sketch_text.stroke-82")}),1.0]])]});
            var Q110;
            Q110=makeQuery(id+"F0.imprint","IMPRINT",FACE,{"disambiguationData":[TD([[makeQuery(id+"F0.imprint","IMPRINT",EDGE,{"derivedFrom":sQuery(id+"F0.wireOp",EDGE,"bde91d3f-1bd3-45ad-82db-db1f5e1f2c44.sketch_text.stroke-0")}),-1.0]])]});
            var Q111;
            Q111=makeQuery(id+"F0.imprint","IMPRINT",FACE,{"disambiguationData":[TD([[makeQuery(id+"F0.imprint","IMPRINT",EDGE,{"derivedFrom":sQuery(id+"F0.wireOp",EDGE,"bde91d3f-1bd3-45ad-82db-db1f5e1f2c44.sketch_text.stroke-40")}),1.0]])]});
            var Q112;
            Q112=makeQuery(id+"F0.imprint","IMPRINT",FACE,{"disambiguationData":[TD([[makeQuery(id+"F0.imprint","IMPRINT",EDGE,{"derivedFrom":sQuery(id+"F0.wireOp",EDGE,"2062883b-def4-4ea2-a975-12661bf533bd.sketch_text.stroke-18")}),-1.0]])]});
            var Q113;
            Q113=makeQuery(id+"F0.imprint","IMPRINT",FACE,{"disambiguationData":[TD([[makeQuery(id+"F0.imprint","IMPRINT",EDGE,{"derivedFrom":sQuery(id+"F0.wireOp",EDGE,"82b4a819-2965-4918-af0a-af63fe75002e.sketch_text.stroke-24")}),-1.0]])]});
            var Q114;
            Q114=makeQuery(id+"F0.imprint","IMPRINT",FACE,{"disambiguationData":[TD([[makeQuery(id+"F0.imprint","IMPRINT",EDGE,{"derivedFrom":sQuery(id+"F0.wireOp",EDGE,"859a48e1-c7f7-4a18-9492-87fe2e6c1c5c.sketch_text.stroke-8")}),1.0]])]});
            var Q115;
            Q115=makeQuery(id+"F0.imprint","IMPRINT",FACE,{"disambiguationData":[TD([[makeQuery(id+"F0.imprint","IMPRINT",EDGE,{"derivedFrom":sQuery(id+"F0.wireOp",EDGE,"d4bc6b6e-f296-4560-aa30-6e7daed0d7fc.sketch_text.stroke-18")}),1.0]])]});
            var Q116;
            Q116=makeQuery(id+"F0.imprint","IMPRINT",FACE,{"disambiguationData":[TD([[makeQuery(id+"F0.imprint","IMPRINT",EDGE,{"derivedFrom":sQuery(id+"F0.wireOp",EDGE,"922ba498-ed72-4b5b-995e-0f6d56ec32e2.sketch_text.stroke-129")}),1.0]])]});
            var Q117;
            Q117=makeQuery(id+"F0.imprint","IMPRINT",FACE,{"disambiguationData":[TD([[makeQuery(id+"F0.imprint","IMPRINT",EDGE,{"derivedFrom":sQuery(id+"F0.wireOp",EDGE,"dd86ef6c-a984-4585-901d-e8c8913c4099.sketch_text.stroke-93")}),1.0]])]});
            var Q118;
            Q118=makeQuery(id+"F0.imprint","IMPRINT",FACE,{"disambiguationData":[TD([[makeQuery(id+"F0.imprint","IMPRINT",EDGE,{"derivedFrom":sQuery(id+"F0.wireOp",EDGE,"922ba498-ed72-4b5b-995e-0f6d56ec32e2.sketch_text.stroke-33")}),1.0]])]});
            var Q119;
            Q119=makeQuery(id+"F0.imprint","IMPRINT",FACE,{"disambiguationData":[TD([[makeQuery(id+"F0.imprint","IMPRINT",EDGE,{"derivedFrom":sQuery(id+"F0.wireOp",EDGE,"2062883b-def4-4ea2-a975-12661bf533bd.sketch_text.stroke-37")}),1.0]])]});
            var Q120;
            Q120=makeQuery(id+"F0.imprint","IMPRINT",FACE,{"disambiguationData":[TD([[makeQuery(id+"F0.imprint","IMPRINT",EDGE,{"derivedFrom":sQuery(id+"F0.wireOp",EDGE,"d4bc6b6e-f296-4560-aa30-6e7daed0d7fc.sketch_text.stroke-48")}),1.0]])]});
            var Q121;
            Q121=makeQuery(id+"F0.imprint","IMPRINT",FACE,{"disambiguationData":[TD([[makeQuery(id+"F0.imprint","IMPRINT",EDGE,{"derivedFrom":sQuery(id+"F0.wireOp",EDGE,"922ba498-ed72-4b5b-995e-0f6d56ec32e2.sketch_text.stroke-138")}),1.0]])]});
            var Q122;
            Q122=makeQuery(id+"F0.imprint","IMPRINT",FACE,{"disambiguationData":[TD([[makeQuery(id+"F0.imprint","IMPRINT",EDGE,{"derivedFrom":sQuery(id+"F0.wireOp",EDGE,"922ba498-ed72-4b5b-995e-0f6d56ec32e2.sketch_text.stroke-92")}),-1.0]])]});
            var Q123;
            Q123=makeQuery(id+"F0.imprint","IMPRINT",FACE,{"disambiguationData":[TD([[makeQuery(id+"F0.imprint","IMPRINT",EDGE,{"derivedFrom":sQuery(id+"F0.wireOp",EDGE,"dd86ef6c-a984-4585-901d-e8c8913c4099.sketch_text.stroke-30")}),-1.0]])]});
            var Q124;
            Q124=makeQuery(id+"F0.imprint","IMPRINT",FACE,{"disambiguationData":[TD([[makeQuery(id+"F0.imprint","IMPRINT",EDGE,{"derivedFrom":sQuery(id+"F0.wireOp",EDGE,"E37.bottom")}),1.0]])]});
            var Q125;
            Q125=makeQuery(id+"F0.imprint","IMPRINT",FACE,{"disambiguationData":[TD([[makeQuery(id+"F0.imprint","IMPRINT",EDGE,{"derivedFrom":sQuery(id+"F0.wireOp",EDGE,"E43")}),1.0]])]});
            var Q126;
            Q126=makeQuery(id+"F0.imprint","IMPRINT",FACE,{"disambiguationData":[TD([[makeQuery(id+"F0.imprint","IMPRINT",EDGE,{"derivedFrom":sQuery(id+"F0.wireOp",EDGE,"E44.bottom")}),1.0]])]});
            var Q127;
            Q127=makeQuery(id+"F0.imprint","IMPRINT",FACE,{"disambiguationData":[TD([[makeQuery(id+"F0.imprint","IMPRINT",EDGE,{"derivedFrom":sQuery(id+"F0.wireOp",EDGE,"E54")}),1.0]])]});
            var Q128;
            Q128=makeQuery(id+"F0.imprint","IMPRINT",FACE,{"disambiguationData":[TD([[makeQuery(id+"F0.imprint","IMPRINT",EDGE,{"derivedFrom":sQuery(id+"F0.wireOp",EDGE,"E45.bottom")}),1.0]])]});
            var Q129;
            Q129=makeQuery(id+"F0.imprint","IMPRINT",FACE,{"disambiguationData":[TD([[makeQuery(id+"F0.imprint","IMPRINT",EDGE,{"derivedFrom":sQuery(id+"F0.wireOp",EDGE,"E56.bottom")}),1.0]])]});
            var Q130;
            Q130=makeQuery(id+"F0.imprint","IMPRINT",FACE,{"disambiguationData":[TD([[makeQuery(id+"F0.imprint","IMPRINT",EDGE,{"derivedFrom":sQuery(id+"F0.wireOp",EDGE,"E55.bottom")}),-1.0]])]});
            var Q131;
            Q131=makeQuery(id+"F0.imprint","IMPRINT",FACE,{"disambiguationData":[TD([[makeQuery(id+"F0.imprint","IMPRINT",EDGE,{"derivedFrom":sQuery(id+"F0.wireOp",EDGE,"E59.bottom")}),-1.0]])]});
            extrude(context, id + "F1", {"entities" : qUnion([Q0, Q1, Q2, Q3, Q4, Q5, Q6, Q7, Q8, Q9, Q10, Q11, Q12, Q13, Q14, Q15, Q16, Q17, Q18, Q19, Q20, Q21, Q22, Q23, Q24, Q25, Q26, Q27, Q28, Q29, Q30, Q31, Q32, Q33, Q34, Q35, Q36, Q37, Q38, Q39, Q40, Q41, Q42, Q43, Q44, Q45, Q46, Q47, Q48, Q49, Q50, Q51, Q52, Q53, Q54, Q55, Q56, Q57, Q58, Q59, Q60, Q61, Q62, Q63, Q64, Q65, Q66, Q67, Q68, Q69, Q70, Q71, Q72, Q73, Q74, Q75, Q76, Q77, Q78, Q79, Q80, Q81, Q82, Q83, Q84, Q85, Q86, Q87, Q88, Q89, Q90, Q91, Q92, Q93, Q94, Q95, Q96, Q97, Q98, Q99, Q100, Q101, Q102, Q103, Q104, Q105, Q106, Q107, Q108, Q109, Q110, Q111, Q112, Q113, Q114, Q115, Q116, Q117, Q118, Q119, Q120, Q121, Q122, Q123, Q124, Q125, Q126, Q127, Q128, Q129, Q130, Q131]), "oppositeDirection" : true, "depth" : 52 * mm, "offsetDistance" : 25 * mm});
        }
        {
            var Q0;
            Q0=makeQuery(id+"F0.imprint","IMPRINT",FACE,{"disambiguationData":[TD([[makeQuery(id+"F0.imprint","IMPRINT",EDGE,{"derivedFrom":sQuery(id+"F0.wireOp",EDGE,"E44.bottom")}),1.0]])]});
            var Q1;
            Q1=makeQuery(id+"F0.imprint","IMPRINT",FACE,{"disambiguationData":[TD([[makeQuery(id+"F0.imprint","IMPRINT",EDGE,{"derivedFrom":sQuery(id+"F0.wireOp",EDGE,"E37.bottom")}),1.0]])]});
            var Q2;
            Q2=makeQuery(id+"F0.imprint","IMPRINT",FACE,{"disambiguationData":[TD([[makeQuery(id+"F0.imprint","IMPRINT",EDGE,{"derivedFrom":sQuery(id+"F0.wireOp",EDGE,"E28.bottom")}),-1.0]])]});
            var Q3;
            Q3=makeQuery(id+"F0.imprint","IMPRINT",FACE,{"disambiguationData":[TD([[makeQuery(id+"F0.imprint","IMPRINT",EDGE,{"derivedFrom":sQuery(id+"F0.wireOp",EDGE,"E27")}),1.0]])]});
            var Q4;
            Q4=makeQuery(id+"F0.imprint","IMPRINT",FACE,{"disambiguationData":[TD([[makeQuery(id+"F0.imprint","IMPRINT",EDGE,{"derivedFrom":sQuery(id+"F0.wireOp",EDGE,"E35")}),1.0]])]});
            var Q5;
            Q5=makeQuery(id+"F0.imprint","IMPRINT",FACE,{"disambiguationData":[TD([[makeQuery(id+"F0.imprint","IMPRINT",EDGE,{"derivedFrom":sQuery(id+"F0.wireOp",EDGE,"E36")}),1.0]])]});
            var Q6;
            Q6=makeQuery(id+"F0.imprint","IMPRINT",FACE,{"disambiguationData":[TD([[makeQuery(id+"F0.imprint","IMPRINT",EDGE,{"derivedFrom":sQuery(id+"F0.wireOp",EDGE,"E1")}),1.0]])]});
            var Q7;
            Q7=makeQuery(id+"F0.imprint","IMPRINT",FACE,{"disambiguationData":[TD([[makeQuery(id+"F0.imprint","IMPRINT",EDGE,{"derivedFrom":sQuery(id+"F0.wireOp",EDGE,"E18")}),1.0]])]});
            var Q8;
            Q8=makeQuery(id+"F0.imprint","IMPRINT",FACE,{"disambiguationData":[TD([[makeQuery(id+"F0.imprint","IMPRINT",EDGE,{"derivedFrom":sQuery(id+"F0.wireOp",EDGE,"E43")}),1.0]])]});
            var Q9;
            Q9=makeQuery(id+"F0.imprint","IMPRINT",FACE,{"disambiguationData":[TD([[makeQuery(id+"F0.imprint","IMPRINT",EDGE,{"derivedFrom":sQuery(id+"F0.wireOp",EDGE,"E17")}),1.0]])]});
            var Q10;
            Q10=makeQuery(id+"F0.imprint","IMPRINT",FACE,{"disambiguationData":[TD([[makeQuery(id+"F0.imprint","IMPRINT",EDGE,{"derivedFrom":sQuery(id+"F0.wireOp",EDGE,"E45.bottom")}),1.0]])]});
            var Q11;
            Q11=makeQuery(id+"F0.imprint","IMPRINT",FACE,{"disambiguationData":[TD([[makeQuery(id+"F0.imprint","IMPRINT",EDGE,{"derivedFrom":sQuery(id+"F0.wireOp",EDGE,"E54")}),1.0]])]});
            var Q12;
            Q12=makeQuery(id+"F0.imprint","IMPRINT",FACE,{"disambiguationData":[TD([[makeQuery(id+"F0.imprint","IMPRINT",EDGE,{"derivedFrom":sQuery(id+"F0.wireOp",EDGE,"E3.bottom")}),1.0]])]});
            var Q13;
            Q13=makeQuery(id+"F0.imprint","IMPRINT",FACE,{"disambiguationData":[TD([[makeQuery(id+"F0.imprint","IMPRINT",EDGE,{"derivedFrom":sQuery(id+"F0.wireOp",EDGE,"E26")}),1.0]])]});
            var Q14;
            Q14=makeQuery(id+"F0.imprint","IMPRINT",FACE,{"disambiguationData":[TD([[makeQuery(id+"F0.imprint","IMPRINT",EDGE,{"derivedFrom":sQuery(id+"F0.wireOp",EDGE,"E25")}),1.0]])]});
            var Q15;
            Q15=makeQuery(id+"F0.imprint","IMPRINT",FACE,{"disambiguationData":[TD([[makeQuery(id+"F0.imprint","IMPRINT",EDGE,{"derivedFrom":sQuery(id+"F0.wireOp",EDGE,"E19.bottom")}),-1.0]])]});
            var Q16;
            Q16=makeQuery(id+"F0.imprint","IMPRINT",FACE,{"disambiguationData":[TD([[makeQuery(id+"F0.imprint","IMPRINT",EDGE,{"derivedFrom":sQuery(id+"F0.wireOp",EDGE,"E2.bottom")}),-1.0]])]});
            var Q17;
            Q17=makeQuery(id+"F0.imprint","IMPRINT",FACE,{"disambiguationData":[TD([[makeQuery(id+"F0.imprint","IMPRINT",EDGE,{"derivedFrom":sQuery(id+"F0.wireOp",EDGE,"E24")}),1.0]])]});
            var Q18;
            Q18=makeQuery(id+"F0.imprint","IMPRINT",FACE,{"disambiguationData":[TD([[makeQuery(id+"F0.imprint","IMPRINT",EDGE,{"derivedFrom":sQuery(id+"F0.wireOp",EDGE,"E59.bottom")}),-1.0]])]});
            extrude(context, id + "F2", {"entities" : qUnion([Q0, Q1, Q2, Q3, Q4, Q5, Q6, Q7, Q8, Q9, Q10, Q11, Q12, Q13, Q14, Q15, Q16, Q17, Q18]), "operationType" : NewBodyOperationType.REMOVE, "oppositeDirection" : true, "depth" : 50 * mm, "offsetDistance" : 25 * mm});
        }
        {
            var Q0;
            Q0=makeQuery(id+"F1.opExtrude","SWEPT_FACE",FACE,{"disambiguationData":[OSD([sQuery(id+"F0.wireOp",EDGE,"E0.top")])]});
            var sketch = newSketch(context, id + "F3", { "sketchPlane" : qUnion([Q0])});
            skText(sketch, "E64", { "text": "3D Tools", "fontName": "RobotoSlab-Regular.ttf"});
            const initialGuessF3  = {"E64": [-0.05937, -0.03397, 1, 0, 0.021]};
            skSetInitialGuess(sketch, initialGuessF3);
            skSolve(sketch);
        }
        {
            var Q0;
            Q0 = qSketchRegion(id + "F3", true);
            extrude(context, id + "F4", {"entities" : qUnion([Q0]), "operationType" : NewBodyOperationType.ADD, "depth" : .5 * mm, "offsetDistance" : 25 * mm});
        }
        {
            var Q0;
            Q0=makeQuery(id+"F0.imprint","IMPRINT",FACE,{"disambiguationData":[TD([[makeQuery(id+"F0.imprint","IMPRINT",EDGE,{"derivedFrom":sQuery(id+"F0.wireOp",EDGE,"E56.bottom")}),1.0]])]});
            var Q1;
            Q1=makeQuery(id+"F0.imprint","IMPRINT",FACE,{"disambiguationData":[TD([[makeQuery(id+"F0.imprint","IMPRINT",EDGE,{"derivedFrom":sQuery(id+"F0.wireOp",EDGE,"E55.bottom")}),-1.0]])]});
            extrude(context, id + "F5", {"entities" : qUnion([Q0, Q1]), "operationType" : NewBodyOperationType.REMOVE, "oppositeDirection" : true, "depth" : 19.5 * mm, "offsetDistance" : 25 * mm});
        }
    });
